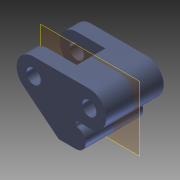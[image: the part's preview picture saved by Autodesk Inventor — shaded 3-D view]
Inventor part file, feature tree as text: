
AUTODESK INVENTOR PART (.ipt)
format: ipt  version: 2011 (Build 150229000, 229)  size: 129,536 bytes
history: native  units: mm (DEFAULTED — no unit token found)
features: extrude x2, hole x2, sketch x2
ambient origin geometry x8: Origin, YZ Plane, XZ Plane, XY Plane, X Axis, Y Axis, Z Axis, Center Point
bodies: Solid1 (feature_tree)
feature tree (6):
  extrude  "Extrusion1"  Depth=8.0mm
  extrude  "Extrusion2"  Depth=1.5mm
  hole  "Hole1"  [1 undecoded]
  hole  "Hole2"  [1 undecoded]
  sketch  "Sketch1"  dims[d0=9.5mm d1=8.0mm]
  sketch  "Sketch2"  dims[d2=31.0mm d3=1.5mm d4=5.5mm d6=9.512966mm d7=6.743535mm d9=32.840229mm d10=16.910363mm d11=32.0mm d12=0.0mm d13=2.0mm d14=16.0mm d15=32.0mm d16=0.0mm d17=10.0mm d18=10.0mm d19=8.0mm d20=6.0mm d21=4.0mm d22=2.0mm d23=90.0deg d24=8.0mm d25=20.594885mm d26=10.0mm d27=10.0mm d28=8.0mm d29=6.0mm d30=4.0mm d31=2.0mm d32=90.0deg d33=8.0mm d34=20.594885mm]
note: 2 required parameter values undecoded (feature->parameter linkage not recoverable at this tier; creation-order binding heuristic only, values carry confidence <= 0.55)
